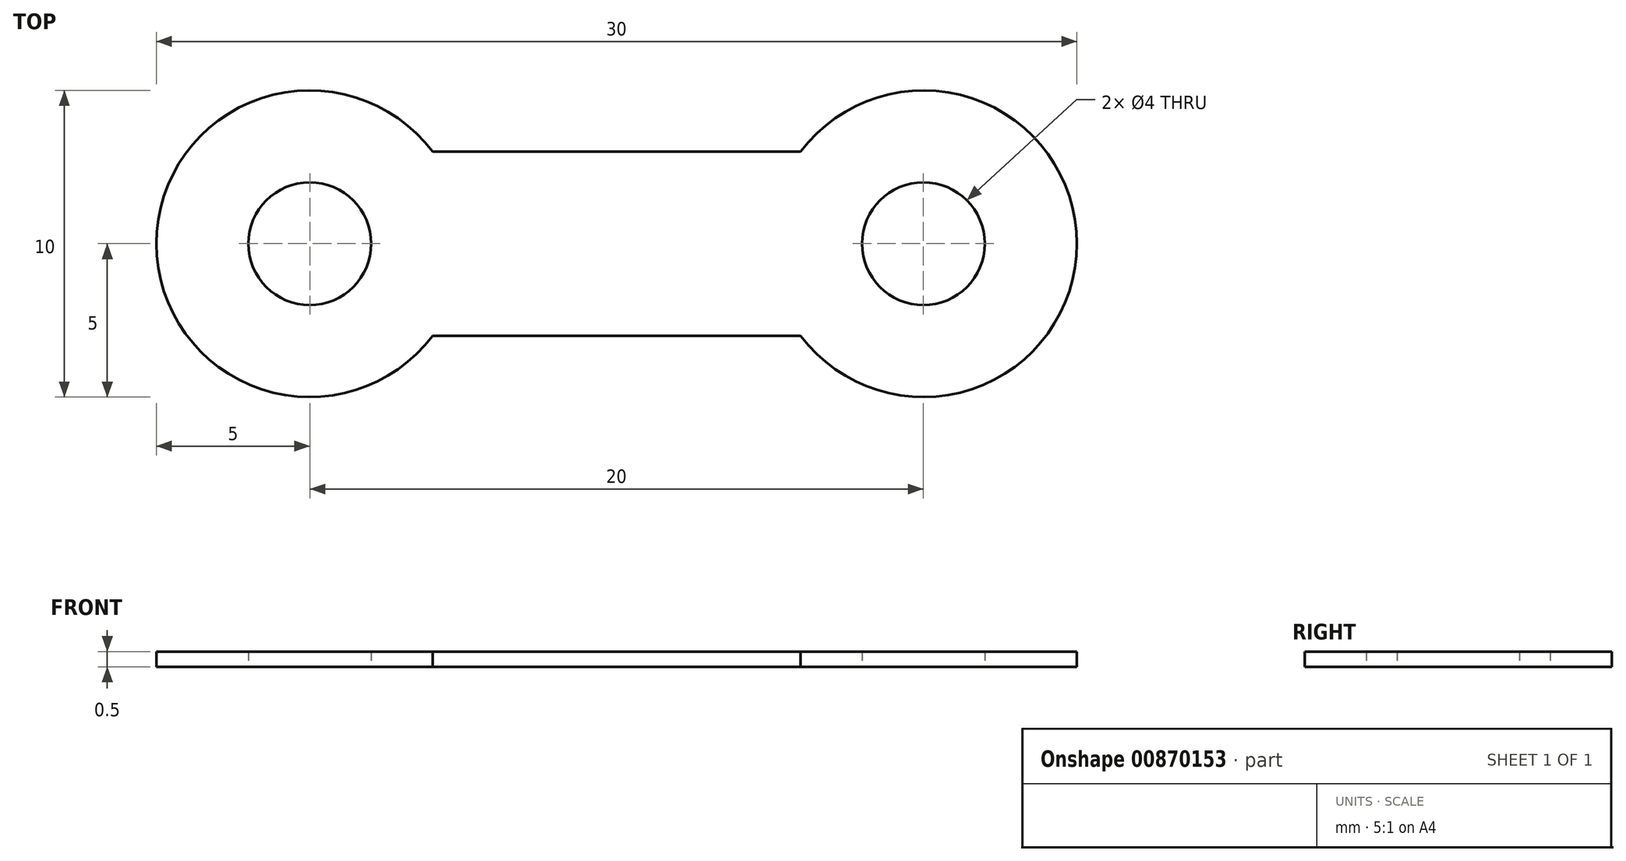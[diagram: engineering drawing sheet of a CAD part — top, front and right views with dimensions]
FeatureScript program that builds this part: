
annotation { "Feature Type Name" : "Feature", "Feature Type Description" : "" }
export const myFeature = defineFeature(function(context is Context, id is Id, definition is map)
    precondition{}
    {
        {
            var Q0;
            Q0=qCreatedBy(makeId("Top.planeOp"),FACE);
            var sketch = newSketch(context, id + "F0", { "sketchPlane" : qUnion([Q0])});
            skCircle(sketch, "E0", {"center": v(-10, 0) * mm, "radius": 5 * mm});
            skCircle(sketch, "E1", {"center": v(10, 0) * mm, "radius": 5 * mm});
            skLineSegment(sketch, "E2", {"start": v(-10, 0) * mm, "end": v(10, 0) * mm, "construction": true});
            skPoint(sketch, "E3", {"position": v(0, 0) * mm});
            skLineSegment(sketch, "E4", {"start": v(-6, 3) * mm, "end": v(6, 3) * mm});
            skLineSegment(sketch, "E5", {"start": v(-6, -3) * mm, "end": v(6, -3) * mm});
            skCircle(sketch, "E6", {"center": v(-10, 0) * mm, "radius": 2 * mm});
            skCircle(sketch, "E7", {"center": v(10, 0) * mm, "radius": 2 * mm});
            skSolve(sketch);
        }
        {
            var Q0;
            {var subQ0=sQuery(id+"F0.wireOp",EDGE,"E0");var subQ1=makeQuery(id+"F0.imprint","INTERSECT",VERTEX,{"derivedFrom":[subQ0,sQuery(id+"F0.wireOp",EDGE,"E4")]});Q0=makeQuery(id+"F0.imprint","IMPRINT",FACE,{"disambiguationData":[TD([[makeQuery(id+"F0.imprint","IMPRINT",EDGE,{"disambiguationData":[TD([[subQ1,-1.0]])],"derivedFrom":subQ0}),1.0]])]});}
            var Q1;
            {var subQ0=sQuery(id+"F0.wireOp",EDGE,"E1");var subQ1=makeQuery(id+"F0.imprint","INTERSECT",VERTEX,{"derivedFrom":[subQ0,sQuery(id+"F0.wireOp",EDGE,"E4")]});Q1=makeQuery(id+"F0.imprint","IMPRINT",FACE,{"disambiguationData":[TD([[makeQuery(id+"F0.imprint","IMPRINT",EDGE,{"disambiguationData":[TD([[subQ1,-1.0]])],"derivedFrom":subQ0}),1.0]])]});}
            var Q2;
            {var subQ0=sQuery(id+"F0.wireOp",EDGE,"E4");Q2=makeQuery(id+"F0.imprint","IMPRINT",FACE,{"disambiguationData":[TD([[makeQuery(id+"F0.imprint","IMPRINT",EDGE,{"derivedFrom":subQ0}),-1.0]])]});}
            extrude(context, id + "F1", {"entities" : qUnion([Q0, Q1, Q2]), "depth" : .5 * mm, "offsetDistance" : 25 * mm, "symmetric" : true});
        }
    });
